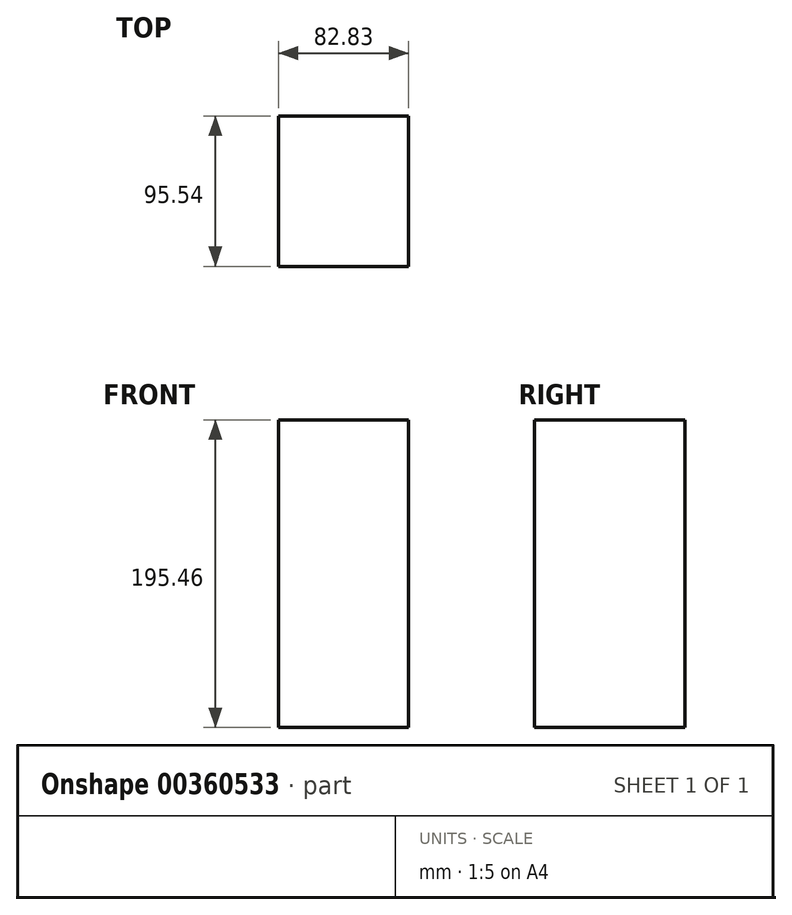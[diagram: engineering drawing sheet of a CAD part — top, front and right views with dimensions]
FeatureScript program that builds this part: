
annotation { "Feature Type Name" : "Feature", "Feature Type Description" : "" }
export const myFeature = defineFeature(function(context is Context, id is Id, definition is map)
    precondition{}
    {
        {
            var Q0;
            Q0=qCreatedBy(makeId("Top.planeOp"),FACE);
            var sketch = newSketch(context, id + "F0", { "sketchPlane" : qUnion([Q0])});
            skLineSegment(sketch, "E0.bottom", {"start": v(43.02, 46.44) * mm, "end": v(-39.81, 46.44) * mm});
            skLineSegment(sketch, "E0.top", {"start": v(43.02, -49.1) * mm, "end": v(-39.81, -49.1) * mm});
            skLineSegment(sketch, "E0.left", {"start": v(43.02, 46.44) * mm, "end": v(43.02, -49.1) * mm});
            skLineSegment(sketch, "E0.right", {"start": v(-39.81, 46.44) * mm, "end": v(-39.81, -49.1) * mm});
            skSolve(sketch);
        }
        {
            var Q0;
            Q0=makeQuery(id+"F0.imprint","IMPRINT",FACE,{"disambiguationData":[TD([[makeQuery(id+"F0.imprint","IMPRINT",EDGE,{"derivedFrom":sQuery(id+"F0.wireOp",EDGE,"E0.bottom")}),1.0]])]});
            extrude(context, id + "F1", {"entities" : qUnion([Q0]), "depth" : 25.4 * mm});
        }
        {
            var Q0;
            Q0=makeQuery(id+"F1.opExtrude","CAP_FACE",FACE,{"disambiguationData":[OSD([sQuery(id+"F0.wireOp",EDGE,"E0.bottom"),sQuery(id+"F0.wireOp",EDGE,"E0.top"),sQuery(id+"F0.wireOp",EDGE,"E0.left"),sQuery(id+"F0.wireOp",EDGE,"E0.right")])],"isStart":false});
            var sketch = newSketch(context, id + "F2", { "sketchPlane" : qUnion([Q0])});
            skSolve(sketch);
        }
        {
            var Q0;
            Q0=makeQuery(id+"F2.imprint","IMPRINT",FACE,{"disambiguationData":[TD([[makeQuery(id+"F2.imprint","IMPRINT",EDGE,{"derivedFrom":makeQuery(id+"F1.opExtrude","CAP_EDGE",EDGE,{"disambiguationData":[OSD([sQuery(id+"F0.wireOp",EDGE,"E0.bottom")])],"isStart":false})}),1.0]])]});
            extrude(context, id + "F3", {"entities" : qUnion([Q0]), "operationType" : NewBodyOperationType.ADD, "depth" : 170.06 * mm});
        }
    });
